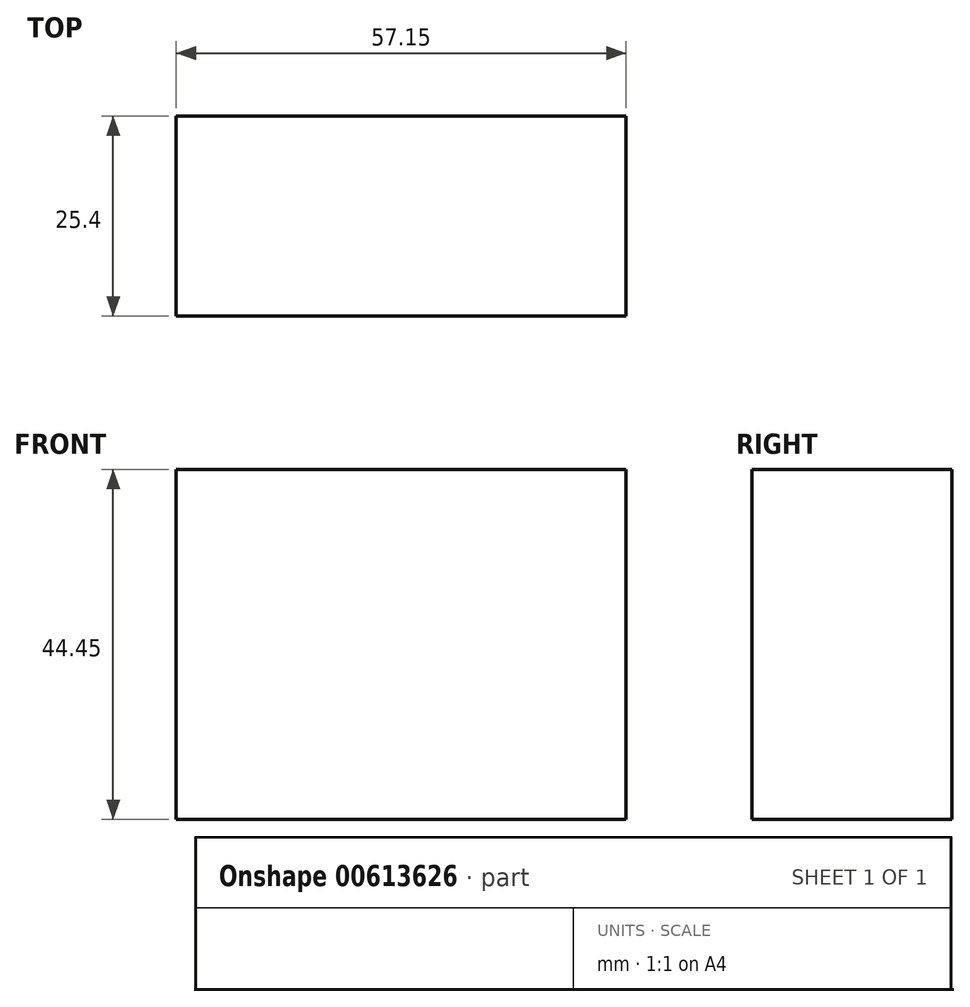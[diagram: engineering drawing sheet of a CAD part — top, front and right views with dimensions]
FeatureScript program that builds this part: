
annotation { "Feature Type Name" : "Feature", "Feature Type Description" : "" }
export const myFeature = defineFeature(function(context is Context, id is Id, definition is map)
    precondition{}
    {
        {
            var Q0;
            Q0=qCreatedBy(makeId("Front.planeOp"),FACE);
            var sketch = newSketch(context, id + "F0", { "sketchPlane" : qUnion([Q0])});
            skLineSegment(sketch, "E0", {"start": v(-74.52, 44.45) * mm, "end": v(-74.52, 0) * mm});
            skLineSegment(sketch, "E1", {"start": v(-74.52, 0) * mm, "end": v(-17.37, 0) * mm});
            skLineSegment(sketch, "E2", {"start": v(-17.37, 0) * mm, "end": v(-17.37, 44.45) * mm});
            skLineSegment(sketch, "E3", {"start": v(-17.37, 44.45) * mm, "end": v(-74.52, 44.45) * mm});
            skSolve(sketch);
        }
        {
            var Q0;
            Q0=makeQuery(id+"F0.imprint","IMPRINT",FACE,{"disambiguationData":[TD([[makeQuery(id+"F0.imprint","IMPRINT",EDGE,{"derivedFrom":sQuery(id+"F0.wireOp",EDGE,"E0")}),1.0]])]});
            extrude(context, id + "F1", {"entities" : qUnion([Q0]), "depth" : 25.4 * mm, "offsetDistance" : 25.4 * mm});
        }
    });
